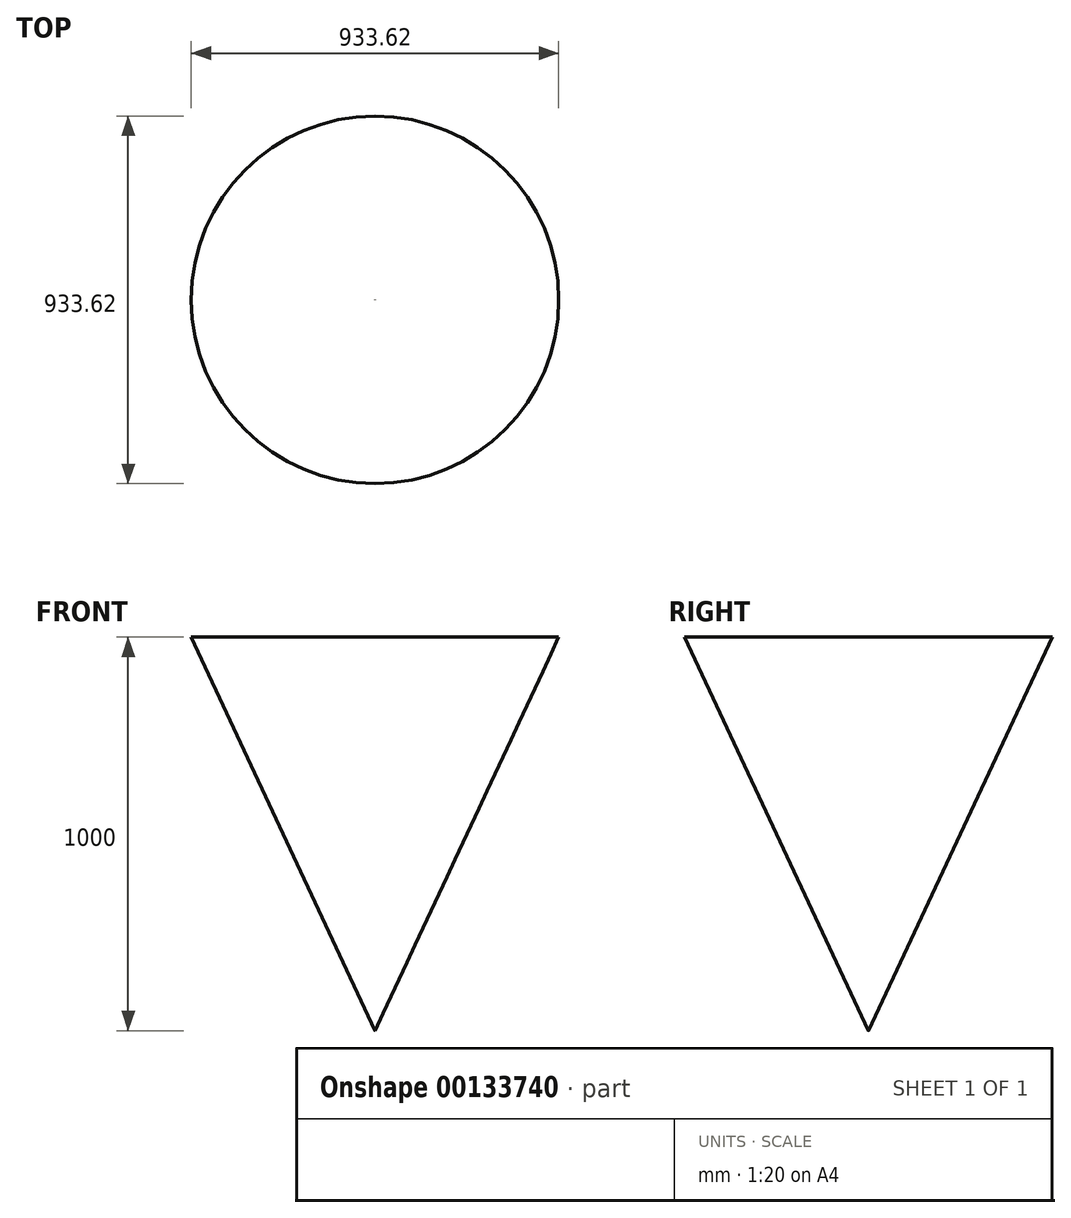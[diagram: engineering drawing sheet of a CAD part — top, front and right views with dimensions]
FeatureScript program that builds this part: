
annotation { "Feature Type Name" : "Feature", "Feature Type Description" : "" }
export const myFeature = defineFeature(function(context is Context, id is Id, definition is map)
    precondition{}
    {
        {
            var Q0;
            Q0=qCreatedBy(makeId("Top.planeOp"),FACE);
            var sketch = newSketch(context, id + "F0", { "sketchPlane" : qUnion([Q0])});
            skCircle(sketch, "E0", {"center": v(0, 0) * mm, "radius": 0.5 * mm});
            skSolve(sketch);
        }
        {
            var Q0;
            Q0 = qSketchRegion(id + "F0", true);
            var Q1;
            Q1=sQuery(id+"F0.wireOp",EDGE,"E0");
            extrude(context, id + "F1", {"entities" : qUnion([Q0]), "surfaceEntities" : qUnion([Q1]), "depth" : 1000 * mm, "hasDraft" : true, "draftAngle" : 25 * degree});
        }
    });
